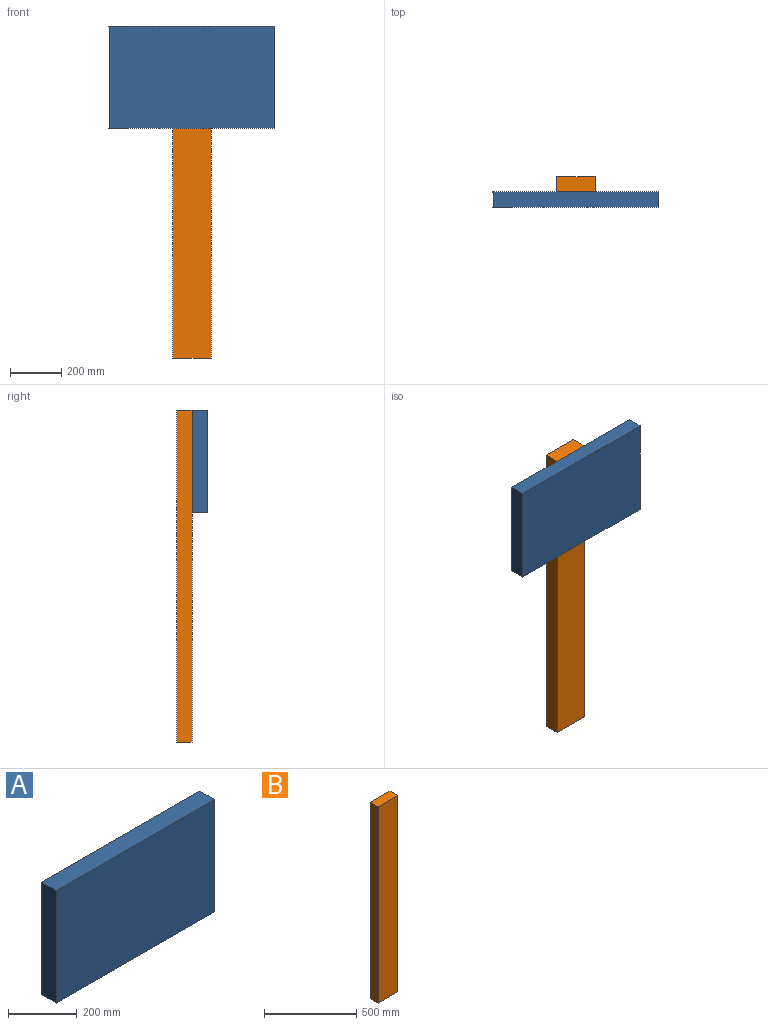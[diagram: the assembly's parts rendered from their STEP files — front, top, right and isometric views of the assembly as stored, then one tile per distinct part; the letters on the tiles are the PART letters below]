
ASSEMBLY  parts=2 mates=1
PART A: 6 faces, bbox 650x60x400 mm
  f0: plane 650x60mm, normal (0,0,1), area 39000mm2, adj f1,f3,f4,f5
  f1: plane 400x60mm, normal (-1,0,0), area 24000mm2, adj f0,f2,f4,f5
  f2: plane 650x60mm, normal (0,0,-1), area 39000mm2, adj f1,f3,f4,f5
  f3: plane 400x60mm, normal (1,0,0), area 24000mm2, adj f0,f2,f4,f5
  f4: plane 650x400mm, normal (0,-1,0), area 260000mm2, adj f0,f1,f2,f3
  f5: plane 650x400mm, normal (0,1,0), area 260000mm2, adj f0,f1,f2,f3
PART B: 6 faces, bbox 150x60x1300 mm
  f0: plane 150x60mm, normal (0,0,1), area 9000mm2, adj f1,f3,f4,f5
  f1: plane 1300x60mm, normal (-1,0,0), area 78000mm2, adj f0,f2,f4,f5
  f2: plane 150x60mm, normal (0,0,-1), area 9000mm2, adj f1,f3,f4,f5
  f3: plane 1300x60mm, normal (1,0,0), area 78000mm2, adj f0,f2,f4,f5
  f4: plane 1300x150mm, normal (0,-1,0), area 195000mm2, adj f0,f1,f2,f3
  f5: plane 1300x150mm, normal (0,1,0), area 195000mm2, adj f0,f1,f2,f3
PLACE A t=(-899.46,225.84,369.78)mm
PLACE B t=(-129.51,285.84,-405.68)mm
MATE fastened A.f5 <-> B.f4  axis (0,1,0) through (-169.2,225.84,646.14)mm
